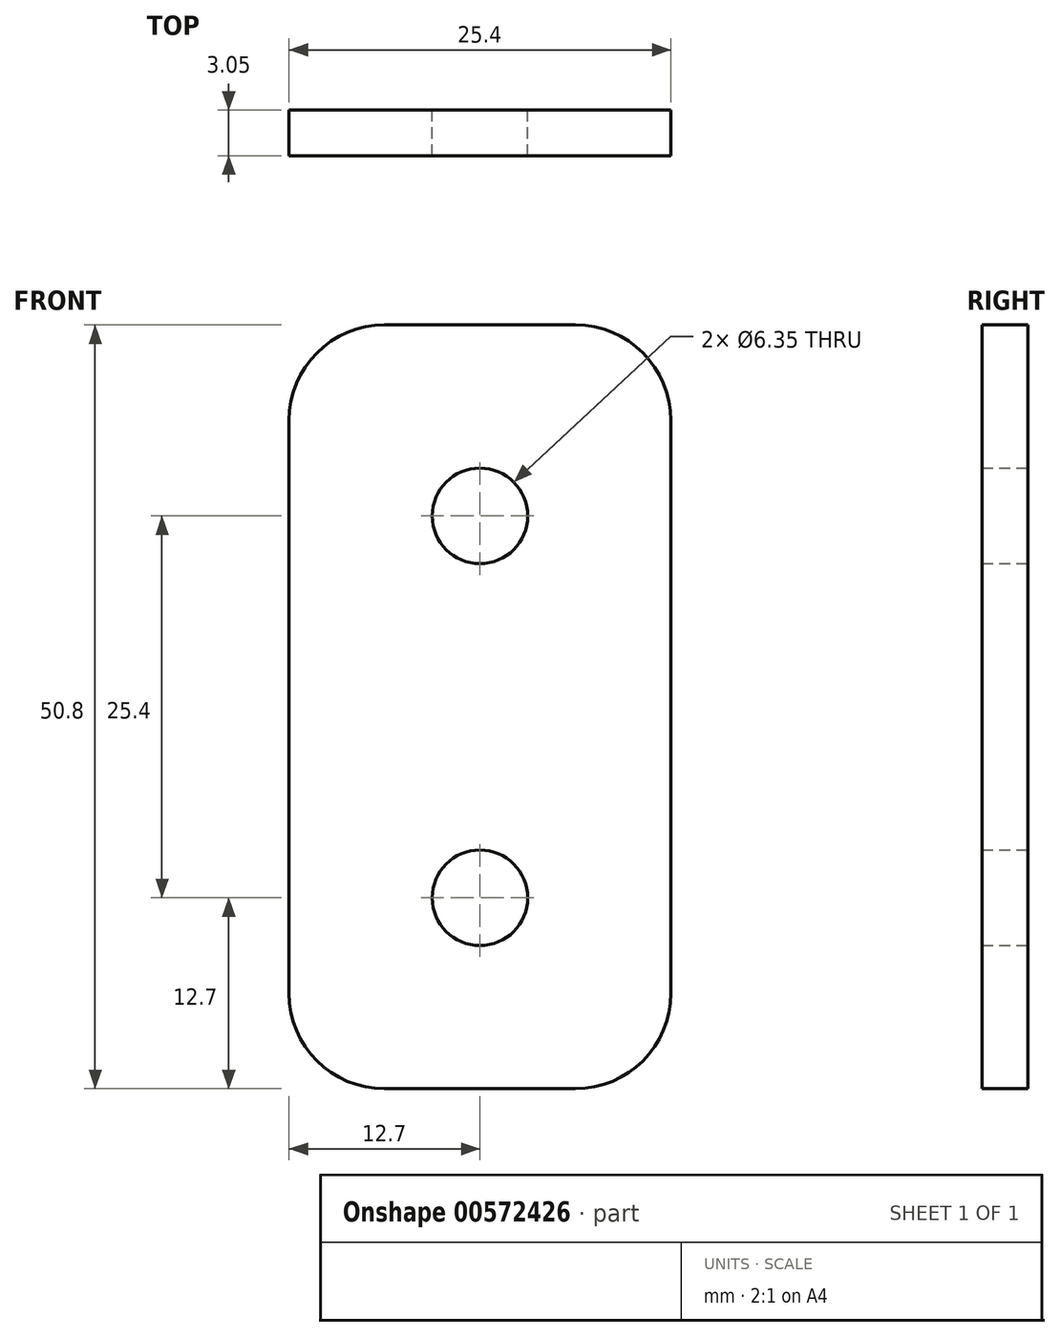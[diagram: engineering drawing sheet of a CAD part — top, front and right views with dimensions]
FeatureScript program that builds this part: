
annotation { "Feature Type Name" : "Feature", "Feature Type Description" : "" }
export const myFeature = defineFeature(function(context is Context, id is Id, definition is map)
    precondition{}
    {
        {
            var Q0;
            Q0=qCreatedBy(makeId("Front.planeOp"),FACE);
            var sketch = newSketch(context, id + "F0", { "sketchPlane" : qUnion([Q0])});
            skLineSegment(sketch, "E0.bottom", {"start": v(6.35, 25.4) * mm, "end": v(-6.35, 25.4) * mm});
            skLineSegment(sketch, "E0.top", {"start": v(6.35, -25.4) * mm, "end": v(-6.35, -25.4) * mm});
            skLineSegment(sketch, "E0.left", {"start": v(12.7, 19.05) * mm, "end": v(12.7, -19.05) * mm});
            skLineSegment(sketch, "E0.right", {"start": v(-12.7, 19.05) * mm, "end": v(-12.7, -19.05) * mm});
            skPoint(sketch, "E0.middle", {"position": v(0, 0) * mm});
            skLineSegment(sketch, "E1", {"start": v(0, 25.4) * mm, "end": v(0, 12.7) * mm, "construction": true});
            skCircle(sketch, "E2", {"center": v(0, 12.7) * mm, "radius": 3.18 * mm});
            skLineSegment(sketch, "E3", {"start": v(0, -25.4) * mm, "end": v(0, -12.7) * mm, "construction": true});
            skCircle(sketch, "E4", {"center": v(0, -12.7) * mm, "radius": 3.18 * mm});
            skPoint(sketch, "E5.visualSharp", {"position": v(-12.7, 25.4) * mm});
            skArc(sketch, "E5.filletArc", {"start": v(-6.35, 25.4) * mm, "mid": v(-10.84, 23.54) * mm, "end": v(-12.7, 19.05) * mm});
            skPoint(sketch, "E6.visualSharp", {"position": v(12.7, 25.4) * mm});
            skArc(sketch, "E6.filletArc", {"start": v(12.7, 19.05) * mm, "mid": v(10.84, 23.54) * mm, "end": v(6.35, 25.4) * mm});
            skPoint(sketch, "E7.visualSharp", {"position": v(-12.7, -25.4) * mm});
            skArc(sketch, "E7.filletArc", {"start": v(-12.7, -19.05) * mm, "mid": v(-10.84, -23.54) * mm, "end": v(-6.35, -25.4) * mm});
            skPoint(sketch, "E8.visualSharp", {"position": v(12.7, -25.4) * mm});
            skArc(sketch, "E8.filletArc", {"start": v(6.35, -25.4) * mm, "mid": v(10.84, -23.54) * mm, "end": v(12.7, -19.05) * mm});
            skSolve(sketch);
        }
        {
            var Q0;
            Q0 = qSketchRegion(id + "F0", true);
            extrude(context, id + "F1", {"entities" : qUnion([Q0]), "depth" : 3.05 * mm, "offsetDistance" : 25.4 * mm});
        }
    });
